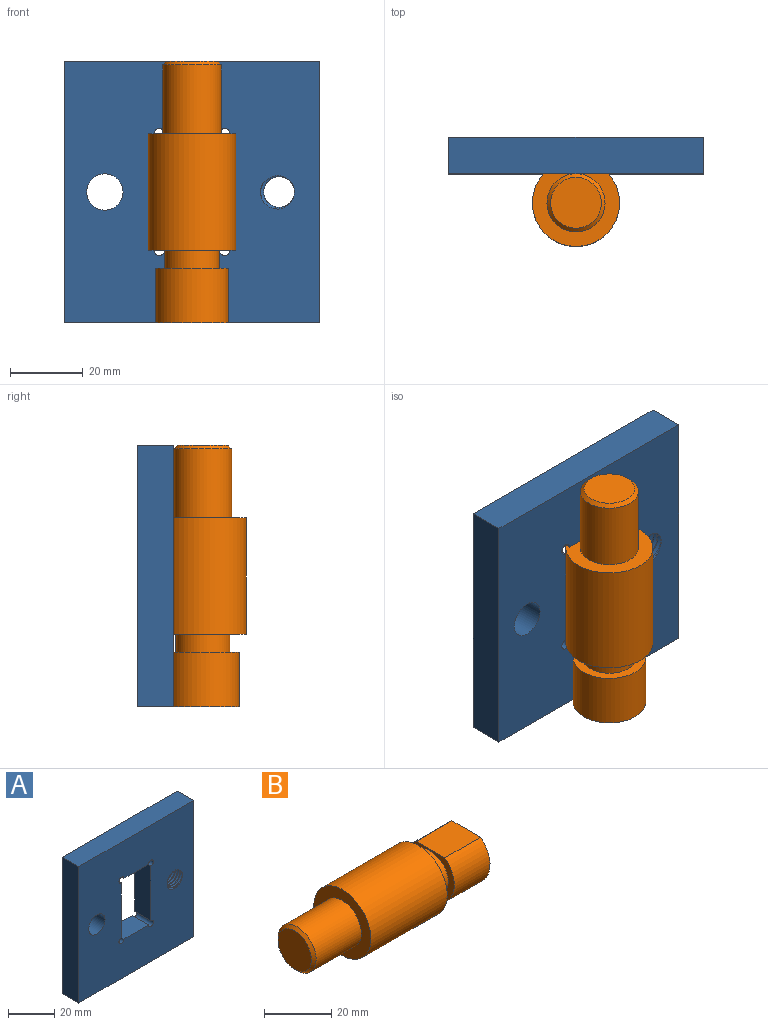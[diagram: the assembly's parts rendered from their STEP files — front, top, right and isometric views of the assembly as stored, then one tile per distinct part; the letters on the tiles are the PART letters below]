
ASSEMBLY  parts=2 mates=1
PART A: 19 faces, bbox 70.4x11.8x72.4 mm
  f0: plane 70x10mm, normal (0,0,1), area 700mm2, adj f1,f12,f13,f14
  f1: plane 72x10mm, normal (-1,0,0), area 720mm2, adj f0,f2,f13,f14
  f2: plane 70x10mm, normal (0,0,-1), area 700mm2, adj f1,f12,f13,f14
  f3: plane 15x10mm, normal (0,0,1), area 150mm2, adj f4,f10,f13,f14
  f4: cylinder r=1.5mm len=10mm, axis (0,1,0), area 70.7mm2, adj f3,f5,f13,f14
  f5: plane 29x10mm, normal (1,0,0), area 290mm2, adj f4,f6,f13,f14
  f6: cylinder r=1.5mm len=10mm, axis (0,1,0), area 70.7mm2, adj f5,f7,f13,f14
  f7: plane 15x10mm, normal (0,0,-1), area 150mm2, adj f6,f8,f13,f14
  f8: cylinder r=1.5mm len=10mm, axis (0,1,0), area 70.7mm2, adj f7,f9,f13,f14
  f9: plane 29x10mm, normal (-1,0,0), area 290mm2, adj f8,f10,f13,f14
  f10: cylinder r=1.5mm len=10mm, axis (0,1,0), area 70.7mm2, adj f3,f9,f13,f14
  f11: cylinder r=5mm len=10mm, axis (0,1,0), area 314.2mm2, adj f13,f14
  f12: plane 72x10mm, normal (1,0,0), area 720mm2, adj f0,f2,f13,f14
  f13: plane 72.44x70.44mm, normal (0,-1,0), area 4297.2mm2, adj f0,f1,f2,f3,f4,f5,f6,f7
  f14: plane 72.44x70.44mm, normal (0,1,0), area 4297.2mm2, adj f0,f1,f2,f3,f4,f5,f6,f7
  f15: bspline ~11.69x11.22mm, area 180.3mm2, adj f13,f14,f17,f18
  f16: bspline ~11.69x11.22mm, area 184.5mm2, adj f13,f14,f17,f18
  f17: bspline ~11.85x10.69mm, area 46.1mm2, adj f13,f14,f15,f16
  f18: cylinder r=4.25mm len=10mm, axis (0,-1,0), area 128.7mm2, adj f13,f14,f15,f16
PART B: 11 faces, bbox 72x24x24 mm
  f0: plane 20x18mm, normal (1,0,0), area 297.8mm2, adj f1,f10
  f1: cylinder r=10mm len=20mm, axis (-1,0,0), area 749.4mm2, adj f0,f2,f10
  f2: plane 20x18mm, normal (-1,0,0), area 121.1mm2, adj f1,f3,f10
  f3: cylinder r=7.5mm len=15mm, axis (-1,0,0), area 235.6mm2, adj f2,f4
  f4: plane 24x24mm, normal (1,0,0), area 275.7mm2, adj f3,f5
  f5: cylinder r=12mm len=32mm, axis (-1,0,0), area 2412.7mm2, adj f4,f6
  f6: plane 24x24mm, normal (-1,0,0), area 251.3mm2, adj f5,f7
  f7: cylinder r=8mm len=19mm, axis (-1,0,0), area 955mm2, adj f6,f9
  f8: plane 14x14mm, normal (-1,0,0), area 153.9mm2, adj f9
  f9: cone r=7mm half-angle=45deg, axis (1,0,0), area 66.6mm2, adj f7,f8
  f10: plane 15x12mm, normal (0,0,1), area 180mm2, adj f0,f1,f2
PLACE A t=(-75.06,2.68,37.85)mm fixed
PLACE B rot(axis=(-0.58,0.58,0.58),120deg) t=(-40.06,-15.32,109.85)mm
MATE fastened A.f2 <-> B.f0  axis (0,0,-1) through (-40.06,-7.32,37.85)mm
